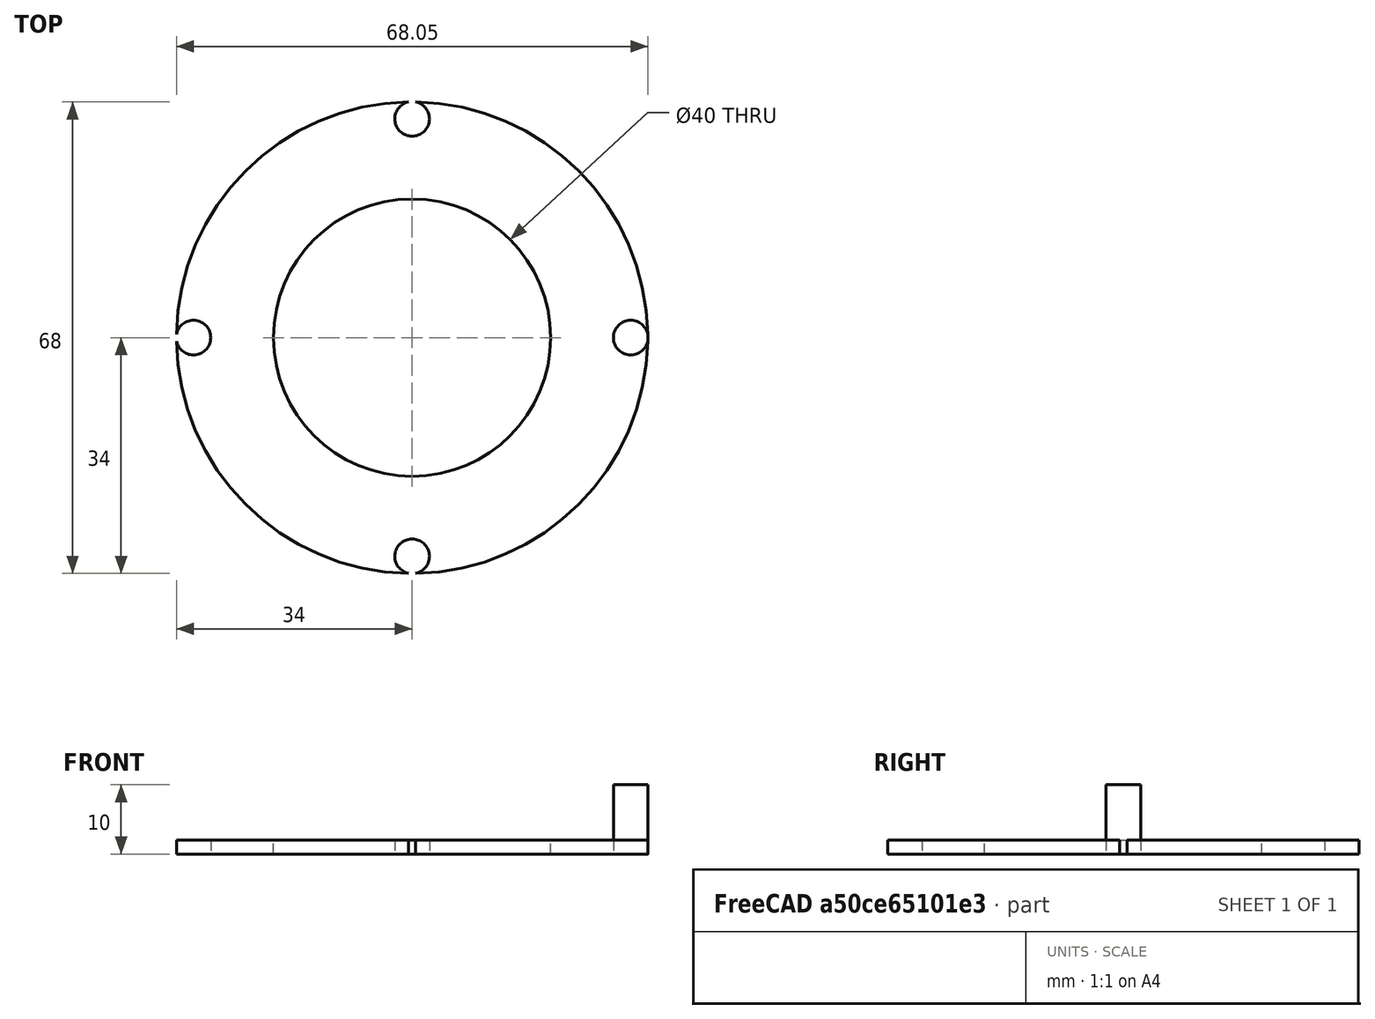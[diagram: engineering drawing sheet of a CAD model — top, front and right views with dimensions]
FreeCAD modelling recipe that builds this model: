
FCSTD DOCUMENT  (FreeCAD 1.0R1.0rc2)
Label: LanternAdapterRingE27
License: All rights reserved
LicenseURL: http://en.wikipedia.org/wiki/All_rights_reserved
objects: Part::FeaturePython×2, Part::Cylinder×1, Part::Cut×1
note: 3 computed .brp shape members not serialized (recipe doc carries the construction recipe); baked Part::Feature solids carry a one-line shape summary decoded from their .brp

FEATURE [Part::FeaturePython] Tube  # WARN: FeaturePython — macro-defined, semantics opaque (R4)
  AttacherType = Attacher::AttachEngine3D
  Height = 2
  InnerRadius = 20
  OuterRadius = 34
FEATURE [Part::Cylinder] Cylinder
  Angle = 360
  AttacherType = Attacher::AttachEngine3D
  FirstAngle = 0
  Height = 10
  Placement = pos=(31.55,0,0) rot=(0,0,1;0rad)
  Radius = 2.5
  SecondAngle = 0
FEATURE [Part::FeaturePython] Array  # Draft array (typed FeaturePython)
  AlwaysSyncPlacement = false
  Angle = 360
  ArrayType = 1
  Axis = (0,0,1)
  Base = -> Cylinder
  Center = (0,0,0)
  Count = 4
  ExpandArray = false
  Fuse = false
  IntervalAxis = (0,0,0)
  IntervalX = (50,0,0)
  IntervalY = (0,50,0)
  IntervalZ = (0,0,50)
  NumberCircles = 3
  NumberPolar = 4
  NumberX = 2
  NumberY = 2
  NumberZ = 1
  PlacementList = 4 placements: [(31.55,0,0),(7.00551e-15,31.55,0),(-31.55,3.86376e-15,0),(-7.00551e-15,-31.55,0)]
  RadialDistance = 50
  ScaleList = (4) [(1,1,1),(1,1,1),(1,1,1),(1,1,1)]
  Symmetry = 1
  TangentialDistance = 25
FEATURE [Part::Cut] Cut
  Base = -> Tube
  Tool = -> Array
